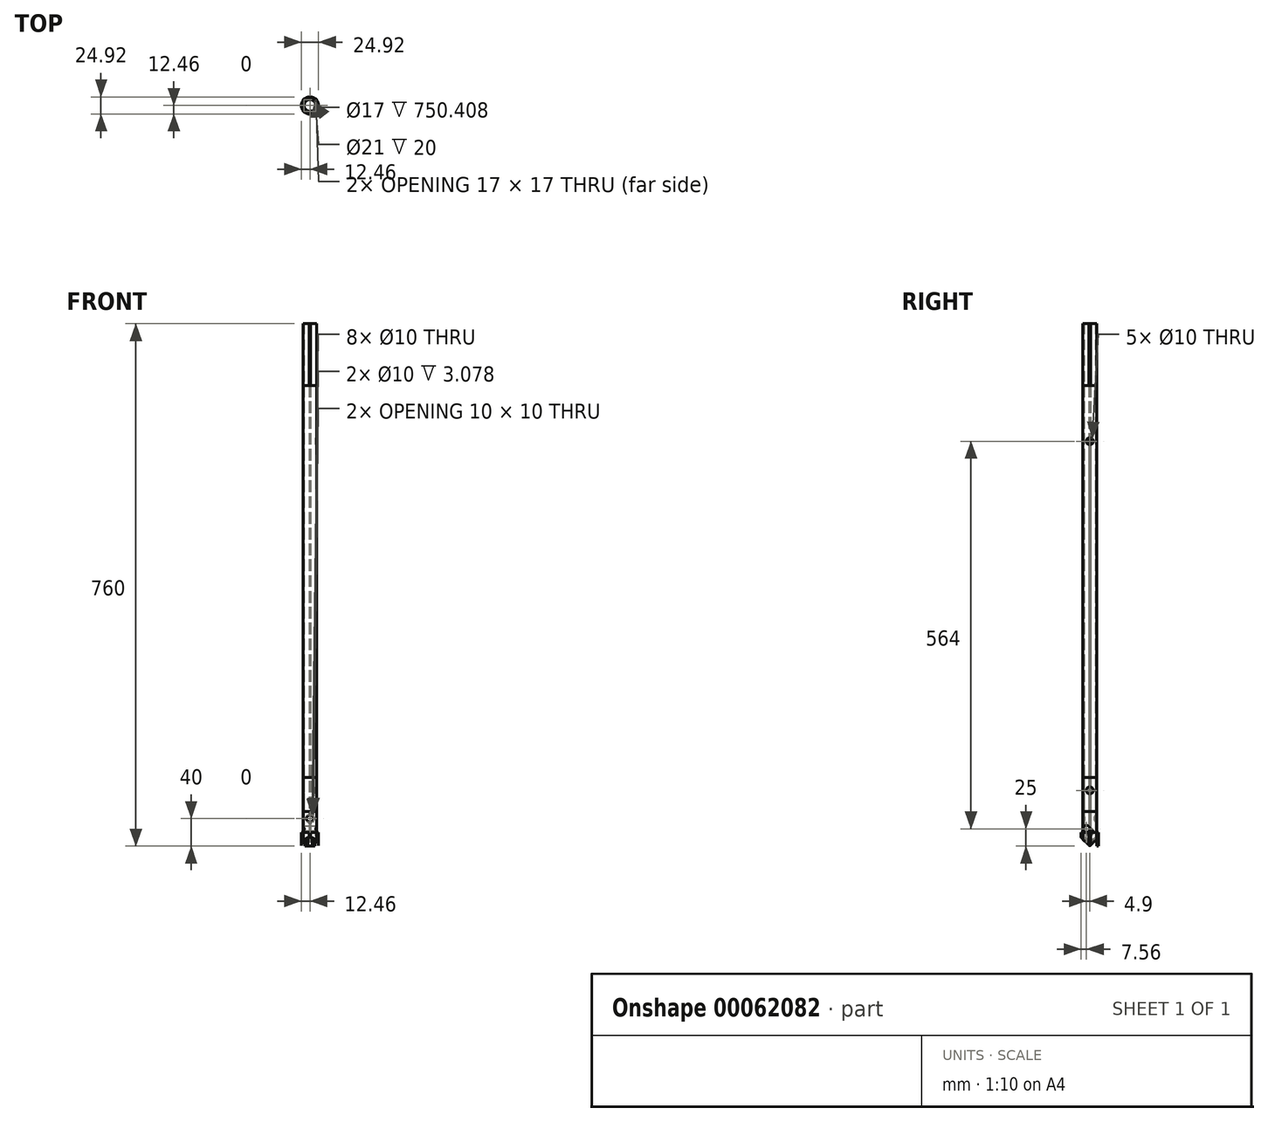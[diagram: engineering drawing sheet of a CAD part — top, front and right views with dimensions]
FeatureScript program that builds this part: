
annotation { "Feature Type Name" : "Feature", "Feature Type Description" : "" }
export const myFeature = defineFeature(function(context is Context, id is Id, definition is map)
    precondition{}
    {
        {
            assignVariable(context, id + "F0", {"name" : "w", "anyValue" : 760});
        }
        {
            var Q0;
            Q0=qCreatedBy(makeId("Top.planeOp"),FACE);
            var sketch = newSketch(context, id + "F1", { "sketchPlane" : qUnion([Q0])});
            skPoint(sketch, "E0.visualSharp", {"position": v(10, 10) * mm});
            skPoint(sketch, "E1.visualSharp", {"position": v(-8.5, -8.5) * mm});
            skPoint(sketch, "E2.visualSharp", {"position": v(-8.5, 8.5) * mm});
            skPoint(sketch, "E3.visualSharp", {"position": v(10, -10) * mm});
            skPoint(sketch, "E4.visualSharp", {"position": v(-10, -10) * mm});
            skLineSegment(sketch, "E5.bottom", {"start": v(-7.5, 10) * mm, "end": v(7.5, 10) * mm});
            skLineSegment(sketch, "E5.top", {"start": v(-7.5, -10) * mm, "end": v(7.5, -10) * mm});
            skLineSegment(sketch, "E5.left", {"start": v(-10, 7.5) * mm, "end": v(-10, -7.5) * mm});
            skLineSegment(sketch, "E5.right", {"start": v(10, 7.5) * mm, "end": v(10, -7.5) * mm});
            skLineSegment(sketch, "E6", {"start": v(-10, 0) * mm, "end": v(10, 0) * mm, "construction": true});
            skPoint(sketch, "E7.visualSharp", {"position": v(8.5, 8.5) * mm});
            skLineSegment(sketch, "E8.0", {"start": v(-8.5, 7.5) * mm, "end": v(-8.5, -7.5) * mm});
            skLineSegment(sketch, "E8.1", {"start": v(-7.5, 8.5) * mm, "end": v(7.5, 8.5) * mm});
            skLineSegment(sketch, "E8.2", {"start": v(8.5, 7.5) * mm, "end": v(8.5, -7.5) * mm});
            skLineSegment(sketch, "E8.3", {"start": v(-7.5, -8.5) * mm, "end": v(7.5, -8.5) * mm});
            skPoint(sketch, "E9.visualSharp", {"position": v(-10, 10) * mm});
            skPoint(sketch, "E10.visualSharp", {"position": v(8.5, -8.5) * mm});
            skArc(sketch, "E3.filletArc", {"start": v(7.5, -10) * mm, "mid": v(9.27, -9.27) * mm, "end": v(10, -7.5) * mm});
            skArc(sketch, "E2.filletArc", {"start": v(-7.5, 8.5) * mm, "mid": v(-8.2, 8.2) * mm, "end": v(-8.5, 7.5) * mm});
            skArc(sketch, "E7.filletArc", {"start": v(8.5, 7.5) * mm, "mid": v(8.2, 8.2) * mm, "end": v(7.5, 8.5) * mm});
            skArc(sketch, "E10.filletArc", {"start": v(7.5, -8.5) * mm, "mid": v(8.2, -8.2) * mm, "end": v(8.5, -7.5) * mm});
            skArc(sketch, "E4.filletArc", {"start": v(-10, -7.5) * mm, "mid": v(-9.27, -9.27) * mm, "end": v(-7.5, -10) * mm});
            skArc(sketch, "E9.filletArc", {"start": v(-7.5, 10) * mm, "mid": v(-9.27, 9.27) * mm, "end": v(-10, 7.5) * mm});
            skArc(sketch, "E0.filletArc", {"start": v(10, 7.5) * mm, "mid": v(9.27, 9.27) * mm, "end": v(7.5, 10) * mm});
            skArc(sketch, "E1.filletArc", {"start": v(-8.5, -7.5) * mm, "mid": v(-8.2, -8.2) * mm, "end": v(-7.5, -8.5) * mm});
            skSolve(sketch);
        }
        {
            var Q0;
            Q0 = qSketchRegion(id + "F1", true);
            extrude(context, id + "F2", {"entities" : qUnion([Q0]), "depth" : (getVariable(context, 'w') - 40 - 40 - 10) * mm});
        }
        {
            var Q0;
            Q0=makeQuery(id+"F2.opExtrude","SWEPT_FACE",FACE,{"disambiguationData":[OSD([sQuery(id+"F1.wireOp",EDGE,"E5.right")])]});
            var sketch = newSketch(context, id + "F3", { "sketchPlane" : qUnion([Q0])});
            skCircle(sketch, "E11", {"center": v(0, 589) * mm, "radius": 5 * mm});
            skCircle(sketch, "E12", {"center": v(0, 81) * mm, "radius": 5 * mm});
            skSolve(sketch);
        }
        {
            var Q0;
            Q0=makeQuery(id+"F3.imprint","IMPRINT",FACE,{"disambiguationData":[TD([[makeQuery(id+"F3.imprint","IMPRINT",EDGE,{"derivedFrom":sQuery(id+"F3.wireOp",EDGE,"E12")}),1.0]])]});
            var Q1;
            Q1=makeQuery(id+"F3.imprint","IMPRINT",FACE,{"disambiguationData":[TD([[makeQuery(id+"F3.imprint","IMPRINT",EDGE,{"derivedFrom":sQuery(id+"F3.wireOp",EDGE,"E11")}),1.0]])]});
            extrude(context, id + "F4", {"entities" : qUnion([Q0, Q1]), "operationType" : NewBodyOperationType.REMOVE, "endBound" : BoundingType.THROUGH_ALL, "oppositeDirection" : true, "depth" : 25 * mm});
        }
        {
            var Q0;
            Q0 = qSketchRegion(id + "F1", true);
            extrude(context, id + "F5", {"entities" : qUnion([Q0]), "depth" : 100 * mm});
        }
        {
            var Q0;
            Q0=makeQuery(id+"F5.opExtrude","SWEPT_FACE",FACE,{"disambiguationData":[OSD([sQuery(id+"F1.wireOp",EDGE,"E5.left")])]});
            var sketch = newSketch(context, id + "F6", { "sketchPlane" : qUnion([Q0])});
            skCircle(sketch, "E13", {"center": v(0, 20) * mm, "radius": 5 * mm});
            skSolve(sketch);
        }
        {
            var Q0;
            Q0=makeQuery(id+"F6.imprint","IMPRINT",FACE,{"disambiguationData":[TD([[makeQuery(id+"F6.imprint","IMPRINT",EDGE,{"derivedFrom":sQuery(id+"F6.wireOp",EDGE,"E13")}),1.0]])]});
            extrude(context, id + "F7", {"entities" : qUnion([Q0]), "operationType" : NewBodyOperationType.REMOVE, "endBound" : BoundingType.THROUGH_ALL, "oppositeDirection" : true, "depth" : 25 * mm});
        }
        {
            var Q0;
            Q0=qCreatedBy(makeId("Right.planeOp"),FACE);
            var sketch = newSketch(context, id + "F8", { "sketchPlane" : qUnion([Q0])});
            skCircle(sketch, "E14", {"center": v(95.47, -129.22) * mm, "radius": 30.84 * mm});
            skCircle(sketch, "E15", {"center": v(0, 0) * mm, "radius": 5 * mm});
            skSolve(sketch);
        }
        {
            var Q0;
            Q0=makeQuery(id+"F8.imprint","IMPRINT",FACE,{"disambiguationData":[TD([[makeQuery(id+"F8.imprint","IMPRINT",EDGE,{"derivedFrom":sQuery(id+"F8.wireOp",EDGE,"E15")}),1.0]])]});
            extrude(context, id + "F9", {"entities" : qUnion([Q0]), "depth" : 45 * mm});
        }
        {
            var Q0;
            Q0 = qSketchRegion(id + "F1", true);
            extrude(context, id + "F10", {"entities" : qUnion([Q0]), "depth" : 50 * mm});
        }
        {
            var Q0;
            Q0=makeQuery(id+"F10.opExtrude","SWEPT_FACE",FACE,{"disambiguationData":[OSD([sQuery(id+"F1.wireOp",EDGE,"E5.left")])]});
            var sketch = newSketch(context, id + "F11", { "sketchPlane" : qUnion([Q0])});
            skCircle(sketch, "E16", {"center": v(4.9, 25) * mm, "radius": 5 * mm});
            skLineSegment(sketch, "E17", {"start": v(4.9, 50) * mm, "end": v(4.9, 0) * mm, "construction": true});
            skSolve(sketch);
        }
        {
            var Q0;
            {var subQ0=sQuery(id+"F11.wireOp",EDGE,"E16");var subQ1=makeQuery(id+"F10.opExtrude","SWEPT_EDGE",EDGE,{"disambiguationData":[OSD([sQuery(id+"F1.wireOp",EDGE,"E5.left"),sQuery(id+"F1.wireOp",EDGE,"E4.filletArc")])]});var subQ2=makeQuery(id+"F11.imprint","INTERSECT",VERTEX,{"disambiguationData":[OD(0.0)],"derivedFrom":[subQ1,subQ0]});Q0=makeQuery(id+"F11.imprint","IMPRINT",FACE,{"disambiguationData":[TD([[makeQuery(id+"F11.imprint","IMPRINT",EDGE,{"disambiguationData":[TD([[subQ2,-1.0]])],"derivedFrom":subQ0}),1.0]])]});}
            var Q1;
            {var subQ0=sQuery(id+"F11.wireOp",EDGE,"E16");var subQ1=makeQuery(id+"F10.opExtrude","SWEPT_EDGE",EDGE,{"disambiguationData":[OSD([sQuery(id+"F1.wireOp",EDGE,"E5.left"),sQuery(id+"F1.wireOp",EDGE,"E4.filletArc")])]});var subQ2=makeQuery(id+"F11.imprint","INTERSECT",VERTEX,{"disambiguationData":[OD(0.0)],"derivedFrom":[subQ1,subQ0]});Q1=makeQuery(id+"F11.imprint","IMPRINT",FACE,{"disambiguationData":[TD([[makeQuery(id+"F11.imprint","IMPRINT",EDGE,{"disambiguationData":[TD([[subQ2,1.0]])],"derivedFrom":subQ0}),1.0]])]});}
            extrude(context, id + "F12", {"entities" : qUnion([Q0, Q1]), "operationType" : NewBodyOperationType.REMOVE, "oppositeDirection" : true, "depth" : 25 * mm});
        }
        {
            var Q0;
            Q0=makeQuery(id+"F10.opExtrude","SWEPT_FACE",FACE,{"disambiguationData":[OSD([sQuery(id+"F1.wireOp",EDGE,"E5.bottom")])]});
            var sketch = newSketch(context, id + "F13", { "sketchPlane" : qUnion([Q0])});
            skLineSegment(sketch, "E18", {"start": v(0, 50) * mm, "end": v(0, 0) * mm, "construction": true});
            skCircle(sketch, "E19", {"center": v(0, 40) * mm, "radius": 3 * mm});
            skCircle(sketch, "E20", {"center": v(0, 10) * mm, "radius": 3 * mm});
            skSolve(sketch);
        }
        {
            var Q0;
            Q0=makeQuery(id+"F13.imprint","IMPRINT",FACE,{"disambiguationData":[TD([[makeQuery(id+"F13.imprint","IMPRINT",EDGE,{"derivedFrom":sQuery(id+"F13.wireOp",EDGE,"E19")}),1.0]])]});
            var Q1;
            Q1=makeQuery(id+"F13.imprint","IMPRINT",FACE,{"disambiguationData":[TD([[makeQuery(id+"F13.imprint","IMPRINT",EDGE,{"derivedFrom":sQuery(id+"F13.wireOp",EDGE,"E20")}),1.0]])]});
            var Q2;
            Q2=sQuery(id+"F13.wireOp",EDGE,"E19");
            var Q3;
            Q3=sQuery(id+"F13.wireOp",EDGE,"E20");
            extrude(context, id + "F14", {"entities" : qUnion([Q0, Q1]), "operationType" : NewBodyOperationType.REMOVE, "surfaceEntities" : qUnion([Q2, Q3]), "endBound" : BoundingType.THROUGH_ALL, "oppositeDirection" : true, "depth" : 25 * mm});
        }
        {
            var Q0;
            Q0=qCreatedBy(makeId("Top.planeOp"),FACE);
            var sketch = newSketch(context, id + "F15", { "sketchPlane" : qUnion([Q0])});
            skCircle(sketch, "E21", {"center": v(0, 0) * mm, "radius": 10 * mm});
            skCircle(sketch, "E22.0", {"center": v(0, 0) * mm, "radius": 8.5 * mm});
            skLineSegment(sketch, "E23", {"start": v(-9.95, 1) * mm, "end": v(-9.95, -1) * mm});
            skLineSegment(sketch, "E24", {"start": v(-1, 9.95) * mm, "end": v(1, 9.95) * mm});
            skLineSegment(sketch, "E25", {"start": v(-1, -9.95) * mm, "end": v(1, -9.95) * mm});
            skLineSegment(sketch, "E26", {"start": v(9.95, -1) * mm, "end": v(9.95, 1) * mm});
            skSolve(sketch);
        }
        {
            var Q0;
            Q0=makeQuery(id+"F15.imprint","IMPRINT",FACE,{"disambiguationData":[TD([[makeQuery(id+"F15.imprint","IMPRINT",EDGE,{"derivedFrom":sQuery(id+"F15.wireOp",EDGE,"E22.0")}),-1.0]])]});
            extrude(context, id + "F16", {"entities" : qUnion([Q0]), "depth" : 760 * mm});
        }
        {
            var Q0;
            Q0 = qSketchRegion(id + "F1", true);
            extrude(context, id + "F17", {"entities" : qUnion([Q0]), "depth" : 50 * mm});
        }
        {
            var Q0;
            Q0=makeQuery(id+"F17.opExtrude","SWEPT_FACE",FACE,{"disambiguationData":[OSD([sQuery(id+"F1.wireOp",EDGE,"E5.top")])]});
            var sketch = newSketch(context, id + "F18", { "sketchPlane" : qUnion([Q0])});
            skCircle(sketch, "E27", {"center": v(0, 40) * mm, "radius": 5 * mm});
            skSolve(sketch);
        }
        {
            var Q0;
            Q0=makeQuery(id+"F18.imprint","IMPRINT",FACE,{"disambiguationData":[TD([[makeQuery(id+"F18.imprint","IMPRINT",EDGE,{"derivedFrom":sQuery(id+"F18.wireOp",EDGE,"E27")}),1.0]])]});
            extrude(context, id + "F19", {"entities" : qUnion([Q0]), "operationType" : NewBodyOperationType.REMOVE, "endBound" : BoundingType.THROUGH_ALL, "oppositeDirection" : true, "depth" : 25 * mm});
        }
        {
            var Q0;
            Q0=makeQuery(id+"F17.opExtrude","SWEPT_FACE",FACE,{"disambiguationData":[OSD([sQuery(id+"F1.wireOp",EDGE,"E5.left")])]});
            var sketch = newSketch(context, id + "F20", { "sketchPlane" : qUnion([Q0])});
            skCircle(sketch, "E28", {"center": v(0, 0) * mm, "radius": 10 * mm});
            skSolve(sketch);
        }
        {
            var Q0;
            {var subQ1=sQuery(id+"F1.wireOp",EDGE,"E5.left");var subQ6=makeQuery(id+"F17.opExtrude","CAP_EDGE",EDGE,{"disambiguationData":[OSD([subQ1])],"isStart":true});Q0=makeQuery(id+"F20.imprint","IMPRINT",FACE,{"disambiguationData":[TD([[makeQuery(id+"F20.imprint","IMPRINT",EDGE,{"derivedFrom":subQ6}),-1.0]])]});}
            var Q1;
            {var subQ1=sQuery(id+"F1.wireOp",EDGE,"E5.left");var subQ6=makeQuery(id+"F17.opExtrude","CAP_EDGE",EDGE,{"disambiguationData":[OSD([subQ1])],"isStart":true});Q1=makeQuery(id+"F20.imprint","IMPRINT",FACE,{"disambiguationData":[TD([[makeQuery(id+"F20.imprint","IMPRINT",EDGE,{"derivedFrom":subQ6}),1.0]])]});}
            extrude(context, id + "F21", {"entities" : qUnion([Q0, Q1]), "operationType" : NewBodyOperationType.REMOVE, "endBound" : BoundingType.THROUGH_ALL, "oppositeDirection" : true, "depth" : 25 * mm});
        }
        {
            var Q0;
            Q0=qCreatedBy(makeId("Top.planeOp"),FACE);
            var sketch = newSketch(context, id + "F22", { "sketchPlane" : qUnion([Q0])});
            skCircle(sketch, "E29", {"center": v(0, 0) * mm, "radius": 12.5 * mm});
            skCircle(sketch, "E30.0", {"center": v(0, 0) * mm, "radius": 10.5 * mm});
            skLineSegment(sketch, "E31", {"start": v(-12.46, 1) * mm, "end": v(-12.46, -1) * mm});
            skLineSegment(sketch, "E32", {"start": v(-1, 12.46) * mm, "end": v(1, 12.46) * mm});
            skLineSegment(sketch, "E33", {"start": v(-1, -12.46) * mm, "end": v(1, -12.46) * mm});
            skLineSegment(sketch, "E34", {"start": v(12.46, -1) * mm, "end": v(12.46, 1) * mm});
            skSolve(sketch);
        }
        {
            var Q0;
            Q0=makeQuery(id+"F22.imprint","IMPRINT",FACE,{"disambiguationData":[TD([[makeQuery(id+"F22.imprint","IMPRINT",EDGE,{"derivedFrom":sQuery(id+"F22.wireOp",EDGE,"E30.0")}),-1.0]])]});
            extrude(context, id + "F23", {"entities" : qUnion([Q0]), "depth" : 20 * mm});
        }
        {
            var Q0;
            Q0 = qSketchRegion(id + "F1", true);
            extrude(context, id + "F24", {"entities" : qUnion([Q0]), "depth" : 50 * mm});
        }
        {
            var Q0;
            Q0=makeQuery(id+"F24.opExtrude","SWEPT_FACE",FACE,{"disambiguationData":[OSD([sQuery(id+"F1.wireOp",EDGE,"E5.bottom")])]});
            var sketch = newSketch(context, id + "F25", { "sketchPlane" : qUnion([Q0])});
            skCircle(sketch, "E35", {"center": v(0, 0) * mm, "radius": 12.5 * mm});
            skSolve(sketch);
        }
        {
            var Q0;
            {var subQ1=sQuery(id+"F1.wireOp",EDGE,"E5.bottom");var subQ6=makeQuery(id+"F24.opExtrude","CAP_EDGE",EDGE,{"disambiguationData":[OSD([subQ1])],"isStart":true});Q0=makeQuery(id+"F25.imprint","IMPRINT",FACE,{"disambiguationData":[TD([[makeQuery(id+"F25.imprint","IMPRINT",EDGE,{"derivedFrom":subQ6}),1.0]])]});}
            var Q1;
            {var subQ1=sQuery(id+"F1.wireOp",EDGE,"E5.bottom");var subQ6=makeQuery(id+"F24.opExtrude","CAP_EDGE",EDGE,{"disambiguationData":[OSD([subQ1])],"isStart":true});Q1=makeQuery(id+"F25.imprint","IMPRINT",FACE,{"disambiguationData":[TD([[makeQuery(id+"F25.imprint","IMPRINT",EDGE,{"derivedFrom":subQ6}),-1.0]])]});}
            extrude(context, id + "F26", {"entities" : qUnion([Q0, Q1]), "operationType" : NewBodyOperationType.REMOVE, "endBound" : BoundingType.THROUGH_ALL, "oppositeDirection" : true, "depth" : 25 * mm});
        }
    });
